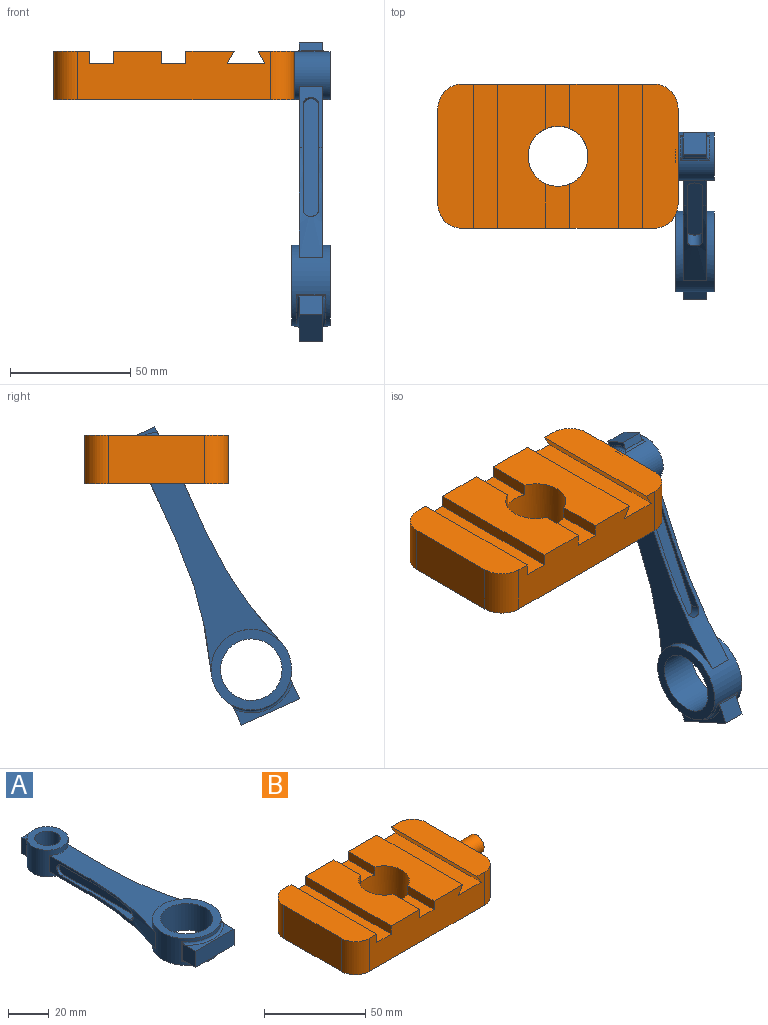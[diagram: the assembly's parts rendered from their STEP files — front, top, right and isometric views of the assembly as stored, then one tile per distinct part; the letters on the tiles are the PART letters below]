
ASSEMBLY  parts=2 mates=1
PART A: 42 faces, bbox 33.7x129.5x16.1 mm
  f0: plane 10x2.64mm, normal (0,0,1), area 18.4mm2, adj f11,f12,f25,f34
  f1: plane 10x2.64mm, normal (0,0,-1), area 18.4mm2, adj f11,f12,f27,f34
  f2: plane 82.69x31.66mm, normal (0,0,1), area 1120mm2, adj f4,f5,f6,f13,f31,f32
  f3: plane 82.69x31.66mm, normal (0,0,-1), area 1120mm2, adj f4,f5,f6,f13,f31,f32
  f4: plane 28x9.6mm, normal (-1,0,0), area 126.7mm2, adj f2,f3,f5,f13,f21,f22,f24
  f5: cylinder r=163.3mm len=54.69mm, axis (0,0,-1), area 326.4mm2, adj f2,f3,f4,f6,f21,f22,f23
  f6: cylinder r=16.8mm len=33.6mm, axis (0,0,-1), area 914.8mm2, adj f2,f3,f5,f16,f17,f28,f29,f30
  f7: plane 10.6x8.73mm, normal (-1,0,0), area 83.7mm2, adj f8,f14,f15,f28,f29,f30
  f8: plane 26.6x9.6mm, normal (0,-1,0), area 255.4mm2, adj f7,f14,f15,f33
  f9: cylinder r=12.8mm len=25.6mm, axis (0,0,-1), area 1286.8mm2, adj f16,f17
  f10: cylinder r=6.25mm len=16mm, axis (0,0,-1), area 628.3mm2, adj f18,f19
  f11: plane 10x9.6mm, normal (0,1,0), area 96mm2, adj f0,f1,f12,f34
  f12: plane 9.95x3.34mm, normal (-1,0,0), area 32.1mm2, adj f0,f1,f11,f25,f26,f27
  f13: cylinder r=10mm len=20mm, axis (0,0,-1), area 731.2mm2, adj f2,f3,f4,f18,f19,f25,f26,f27
  f14: plane 26.6x7.21mm, normal (0,0,1), area 83.7mm2, adj f7,f8,f30,f33
  f15: plane 26.6x7.21mm, normal (0,0,-1), area 83.7mm2, adj f7,f8,f28,f33
  f16: plane 33.6x33.6mm, normal (0,0,-1), area 372mm2, adj f6,f9
  f17: plane 33.6x33.6mm, normal (0,0,1), area 372mm2, adj f6,f9
  f18: plane 20x20mm, normal (0,0,-1), area 191.4mm2, adj f10,f13
  f19: plane 20x20mm, normal (0,0,1), area 191.4mm2, adj f10,f13
  f20: plane 56x6.4mm, normal (-1,0,0), area 349.6mm2, adj f21,f22,f23,f24
  f21: plane 49.6x4.36mm, normal (0,0,1), area 106.8mm2, adj f4,f5,f20,f23,f24
  f22: plane 49.6x4.36mm, normal (0,0,-1), area 106.8mm2, adj f4,f5,f20,f23,f24
  f23: cylinder r=3.2mm len=6.4mm, axis (1,0,0), area 47.8mm2, adj f5,f20,f21,f22
  f24: cylinder r=3.2mm len=6.4mm, axis (-1,0,0), area 16.1mm2, adj f4,f20,f21,f22
  f25: torus R=11.2mm, axis (0,0,1), area 20.3mm2, adj f0,f12,f13,f26,f34,f40
  f26: cylinder r=1.2mm len=12mm, axis (0,0,-1), area 13mm2, adj f12,f13,f25,f27
  f27: torus R=11.2mm, axis (0,0,1), area 20.3mm2, adj f1,f12,f13,f26,f34,f40
  f28: torus R=18mm, axis (0,0,1), area 57.5mm2, adj f6,f7,f15,f29,f33,f41
  f29: cylinder r=1.2mm len=12mm, axis (0,0,-1), area 8.6mm2, adj f6,f7,f28,f30
  f30: torus R=18mm, axis (0,0,1), area 57.5mm2, adj f6,f7,f14,f29,f33,f41
  f31: plane 28x9.6mm, normal (1,0,0), area 126.7mm2, adj f2,f3,f13,f32,f36,f37,f39
  f32: cylinder r=163.3mm len=54.69mm, axis (0,0,-1), area 326.4mm2, adj f2,f3,f6,f31,f36,f37,f38
  f33: plane 10.6x8.73mm, normal (1,0,0), area 83.7mm2, adj f8,f14,f15,f28,f30,f41
  f34: plane 9.95x3.34mm, normal (1,0,0), area 32.1mm2, adj f0,f1,f11,f25,f27,f40
  f35: plane 56x6.4mm, normal (1,0,0), area 349.6mm2, adj f36,f37,f38,f39
  f36: plane 49.6x4.36mm, normal (0,0,1), area 106.8mm2, adj f31,f32,f35,f38,f39
  f37: plane 49.6x4.36mm, normal (0,0,-1), area 106.8mm2, adj f31,f32,f35,f38,f39
  f38: cylinder r=3.2mm len=6.4mm, axis (-1,0,0), area 47.8mm2, adj f32,f35,f36,f37
  f39: cylinder r=3.2mm len=6.4mm, axis (1,0,0), area 16.1mm2, adj f31,f35,f36,f37
  f40: cylinder r=1.2mm len=12mm, axis (0,0,-1), area 13mm2, adj f13,f25,f27,f34
  f41: cylinder r=1.2mm len=12mm, axis (0,0,-1), area 8.6mm2, adj f6,f28,f30,f33
PART B: 28 faces, bbox 115x60x20 mm
  f0: plane 60x15mm, normal (0,0,1), area 857.1mm2, adj f1,f2,f7,f21,f24,f25
  f1: plane 80x20mm, normal (0,1,0), area 1435.6mm2, adj f0,f4,f5,f6,f9,f10,f11,f12
  f2: plane 80x20mm, normal (0,-1,0), area 1435.6mm2, adj f0,f4,f5,f6,f9,f13,f14,f15
  f3: cylinder r=12.5mm len=25mm, axis (0,0,-1), area 1467.9mm2, adj f5,f6,f9,f10,f11,f12,f13,f14
  f4: plane 60x15mm, normal (0,0,1), area 857.1mm2, adj f1,f2,f8,f16,f26,f27
  f5: plane 60x20mm, normal (0,0,1), area 1076.1mm2, adj f1,f2,f3,f10,f13,f17
  f6: plane 60x20mm, normal (0,0,1), area 1076.1mm2, adj f1,f2,f3,f11,f14,f19
  f7: plane 40x20mm, normal (1,0,0), area 721.5mm2, adj f0,f9,f22,f24,f25
  f8: plane 40x20mm, normal (-1,0,0), area 800mm2, adj f4,f9,f26,f27
  f9: plane 100x60mm, normal (0,0,-1), area 5423.3mm2, adj f1,f2,f3,f7,f8,f24,f25,f26
  f10: plane 18.54x5mm, normal (1,0,0), area 92.7mm2, adj f1,f3,f5,f12
  f11: plane 18.54x5mm, normal (-1,0,0), area 92.7mm2, adj f1,f3,f6,f12
  f12: plane 18.54x10mm, normal (0,0,1), area 178.4mm2, adj f1,f3,f10,f11
  f13: plane 18.54x5mm, normal (1,0,0), area 92.7mm2, adj f2,f3,f5,f15
  f14: plane 18.54x5mm, normal (-1,0,0), area 92.7mm2, adj f2,f3,f6,f15
  f15: plane 18.54x10mm, normal (0,0,1), area 178.4mm2, adj f2,f3,f13,f14
  f16: plane 60x5mm, normal (1,0,0), area 300mm2, adj f1,f2,f4,f18
  f17: plane 60x5mm, normal (-1,0,0), area 300mm2, adj f1,f2,f5,f18
  f18: plane 60x10mm, normal (0,0,1), area 600mm2, adj f1,f2,f16,f17
  f19: plane 60x5mm, normal (0.87,0,-0.5), area 346.4mm2, adj f1,f2,f6,f20
  f20: plane 60x15.77mm, normal (0,0,1), area 946.4mm2, adj f1,f2,f19,f21
  f21: plane 60x5mm, normal (-0.87,0,-0.5), area 346.4mm2, adj f0,f1,f2,f20
  f22: cylinder r=5mm len=15mm, axis (-1,0,0), area 471.2mm2, adj f7,f23
  f23: plane 10x10mm, normal (1,0,0), area 78.5mm2, adj f22
  f24: cylinder r=10mm len=20mm, axis (0,0,1), area 314.2mm2, adj f0,f2,f7,f9
  f25: cylinder r=10mm len=20mm, axis (0,0,-1), area 314.2mm2, adj f0,f1,f7,f9
  f26: cylinder r=10mm len=20mm, axis (0,0,1), area 314.2mm2, adj f1,f4,f8,f9
  f27: cylinder r=10mm len=20mm, axis (0,0,-1), area 314.2mm2, adj f2,f4,f8,f9
PLACE A rot(axis=(0.48,0.74,0.48),107.1deg) t=(60.36,28.25,-23.68)mm
PLACE B t=(3.36,67.74,53.82)mm fixed
MATE revolute A.f10 <-> B.f22  axis (-1,0,0) through (68.36,67.74,63.82)mm
